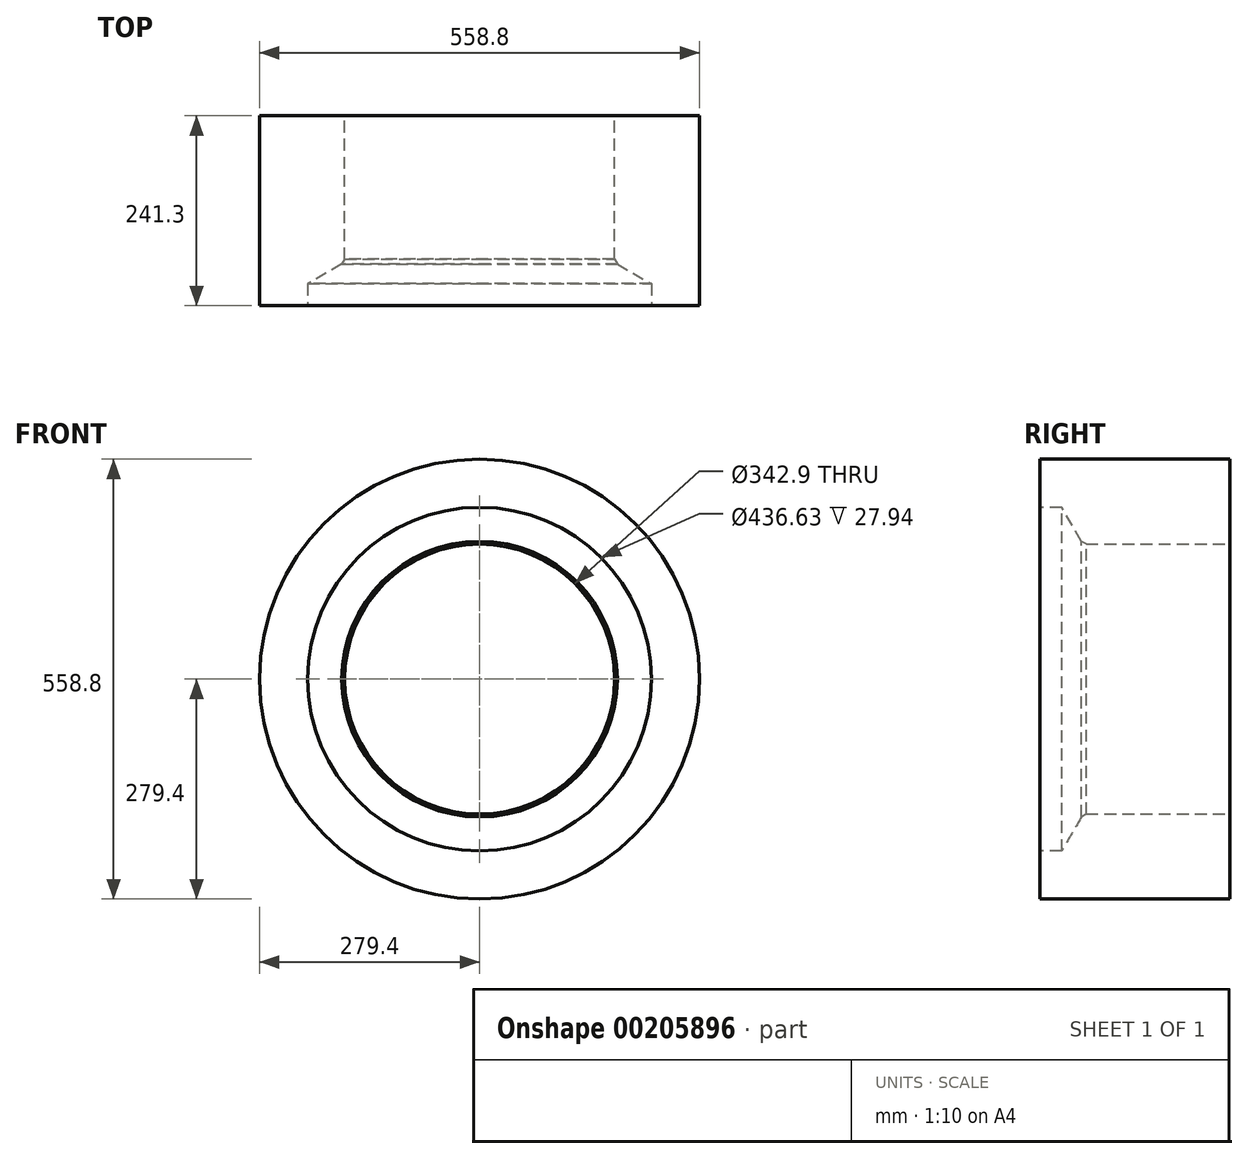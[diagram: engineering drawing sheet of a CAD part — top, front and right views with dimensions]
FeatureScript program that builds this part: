
annotation { "Feature Type Name" : "Feature", "Feature Type Description" : "" }
export const myFeature = defineFeature(function(context is Context, id is Id, definition is map)
    precondition{}
    {
        {
            var Q0;
            Q0=qCreatedBy(makeId("Front.planeOp"),FACE);
            var sketch = newSketch(context, id + "F0", { "sketchPlane" : qUnion([Q0])});
            skCircle(sketch, "E0", {"center": v(0, 0) * mm, "radius": 279.4 * mm});
            skCircle(sketch, "E1", {"center": v(0, 0) * mm, "radius": 171.45 * mm});
            skSolve(sketch);
        }
        {
            var Q0;
            Q0=makeQuery(id+"F0.imprint","IMPRINT",FACE,{"disambiguationData":[TD([[makeQuery(id+"F0.imprint","IMPRINT",EDGE,{"derivedFrom":sQuery(id+"F0.wireOp",EDGE,"E0")}),1.0]])]});
            extrude(context, id + "F1", {"entities" : qUnion([Q0]), "depth" : 241.3 * mm});
        }
        {
            var Q0;
            Q0=qCreatedBy(makeId("Top.planeOp"),FACE);
            var sketch = newSketch(context, id + "F2", { "sketchPlane" : qUnion([Q0])});
            skLineSegment(sketch, "E2", {"start": v(0, 0) * mm, "end": v(0, -244.2) * mm});
            skLineSegment(sketch, "E3", {"start": v(-218.31, -248.94) * mm, "end": v(-218.31, -213.36) * mm});
            skLineSegment(sketch, "E4", {"start": v(-218.31, -213.36) * mm, "end": v(-175, -188.36) * mm});
            skLineSegment(sketch, "E5", {"start": v(-218.31, -248.94) * mm, "end": v(-138.14, -248.94) * mm});
            skLineSegment(sketch, "E6", {"start": v(-138.14, -248.94) * mm, "end": v(-150.7, -174.32) * mm});
            skLineSegment(sketch, "E7", {"start": v(-175, -188.36) * mm, "end": v(-175, -134.53) * mm});
            skLineSegment(sketch, "E8", {"start": v(-171.45, -283.6) * mm, "end": v(-171.45, -261.44) * mm});
            skLineSegment(sketch, "E9", {"start": v(-175, -188.36) * mm, "end": v(-162.83, -167.26) * mm});
            skLineSegment(sketch, "E10", {"start": v(-162.83, -167.26) * mm, "end": v(-150.7, -174.32) * mm});
            skSolve(sketch);
        }
        {
            var Q0;
            Q0=makeQuery(id+"F2.imprint","IMPRINT",FACE,{"disambiguationData":[TD([[makeQuery(id+"F2.imprint","IMPRINT",EDGE,{"derivedFrom":sQuery(id+"F2.wireOp",EDGE,"E3")}),-1.0]])]});
            var Q1;
            Q1=sQuery(id+"F2.wireOp",EDGE,"E2");
            revolve(context, id + "F3", {"operationType" : NewBodyOperationType.REMOVE, "entities" : qUnion([Q0]), "axis" : qUnion([Q1]), "revolveType" : RevolveType.FULL, "oppositeDirection" : true});
        }
    });
